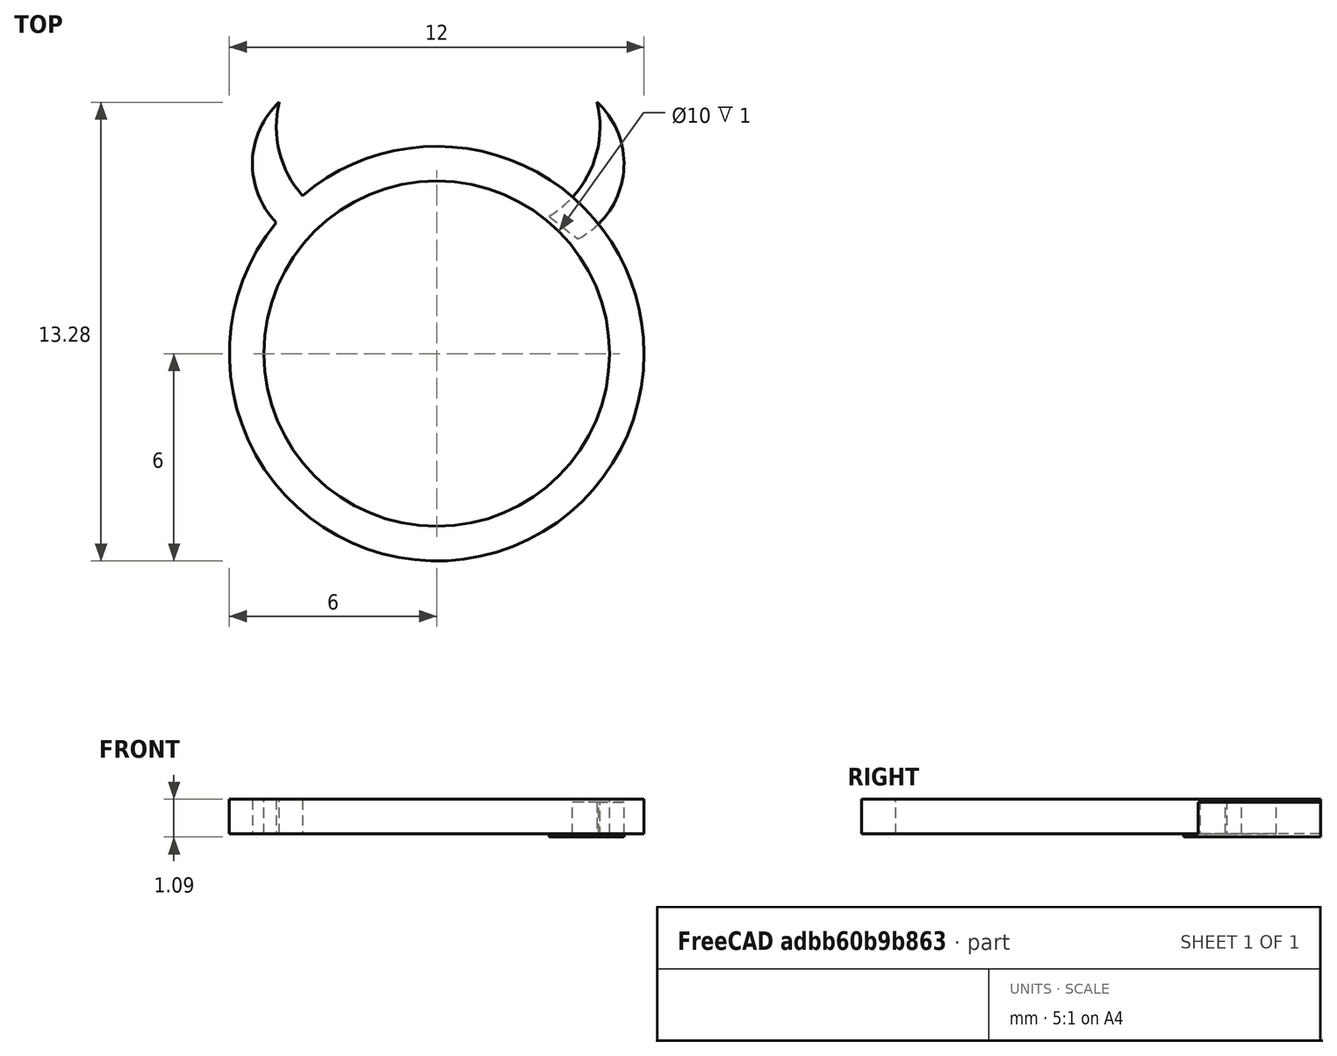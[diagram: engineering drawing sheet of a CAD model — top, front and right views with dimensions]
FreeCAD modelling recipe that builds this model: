
FCSTD DOCUMENT  (FreeCAD 0.20R29177 +233 (Git))
Label: anillo_diablo
License: All rights reserved
LicenseURL: http://en.wikipedia.org/wiki/All_rights_reserved
objects: Part::Extrusion×3, Sketcher::SketchObject×2, Part::FeaturePython×1, Part::MultiFuse×1
note: 7 computed .brp shape members not serialized (recipe doc carries the construction recipe); baked Part::Feature solids carry a one-line shape summary decoded from their .brp

FEATURE [Part::FeaturePython] Tube  # WARN: FeaturePython — macro-defined, semantics opaque (R4)
  AttacherType = Attacher::AttachEngine3D
  Height = 1
  InnerRadius = 5
  OuterRadius = 6
  Placement = pos=(-1,0,0) rot=(0,0,1;0rad)
FEATURE [Sketcher::SketchObject] Sketch
  FullyConstrained = false
  sketch-geometry (3):
    g0: ArcOfCircle CenterX=-3.89539 CenterY=5.49581 CenterZ=0 NormalX=0 NormalY=0 NormalZ=1 AngleXU=0 Radius=2.43805 StartAngle=2.31927 EndAngle=4.24405
    g1: ArcOfCircle CenterX=-2.62591 CenterY=6.56949 CenterZ=0 NormalX=0 NormalY=0 NormalZ=1 AngleXU=0 Radius=3.01411 StartAngle=2.90286 EndAngle=4.1771
    g2: LineSegment StartX=-4.99594 StartY=3.3203 StartZ=0 EndX=-4.16339 EndY=3.977 EndZ=0
  constraints (3):
    c: Coincident(g1,g0)
    c: Coincident(g2,g0)
    c: Coincident(g2,g1)
FEATURE [Part::Extrusion] Extrude
  Base = -> Sketch
  Dir = (0,0,1)
  DirMode = 2
  FaceMakerClass = Part::FaceMakerBullseye
  LengthFwd = 1
  LengthRev = 0
  Solid = true
  Symmetric = false
FEATURE [Part::Extrusion] Extrude001
  Base = -> Sketch
  Dir = (0,0,1)
  DirMode = 2
  FaceMakerClass = Part::FaceMakerBullseye
  LengthFwd = 1
  LengthRev = 0
  Solid = true
  Symmetric = false
FEATURE [Sketcher::SketchObject] Sketch001
  FullyConstrained = false
  sketch-geometry (3):
    g0: ArcOfCircle CenterX=-3.89539 CenterY=5.49581 CenterZ=0 NormalX=0 NormalY=0 NormalZ=1 AngleXU=0 Radius=2.43805 StartAngle=2.31927 EndAngle=4.24405
    g1: ArcOfCircle CenterX=-2.62591 CenterY=6.56949 CenterZ=0 NormalX=0 NormalY=0 NormalZ=1 AngleXU=0 Radius=3.01411 StartAngle=2.90286 EndAngle=4.1771
    g2: LineSegment StartX=-4.99594 StartY=3.3203 StartZ=0 EndX=-4.16339 EndY=3.977 EndZ=0
  constraints (3):
    c: Coincident(g1,g0)
    c: Coincident(g2,g0)
    c: Coincident(g2,g1)
FEATURE [Part::Extrusion] Extrude002
  Base = -> Sketch001
  Dir = (0,0,1)
  DirMode = 2
  FaceMakerClass = Part::FaceMakerBullseye
  LengthFwd = 1
  LengthRev = 0
  Placement = pos=(-1.91421,0,0.914214) rot=(0,1,0;3.14159rad)
  Solid = true
  Symmetric = false
FEATURE [Part::MultiFuse] Fusion
  Shapes = -> [Extrude002,Extrude001,Extrude,Tube]
